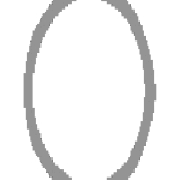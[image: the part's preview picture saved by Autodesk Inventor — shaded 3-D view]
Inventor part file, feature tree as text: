
AUTODESK INVENTOR PART (.ipt)
format: ipt  version: 2021 (Build 250183000, 183)  size: 125,952 bytes
history: native  units: in
note: dims shown in document units (in); Inventor stores cm internally (conversion verified against a paired STEP export)
features: other x4, plane x3, sketch x3, split x2
ambient origin geometry x8: Origin, YZ Plane, XZ Plane, XY Plane, X Axis, Y Axis, Z Axis, Center Point
bodies: Solid1 (feature_tree), Body (feature_tree)
feature tree (12):
  other  "Driven Length"
  other  "Frame Generator"
  other  "Start Plane"
  other  "End Plane"
  plane  "Work Plane5"
  split  "Split1"
  plane  "Work Plane6"
  split  "Split2"
  sketch  "Sketch"  dims[d2=5.831in d4=-0.2406in d5=5.831in d6=0.12in d7=0.0in d10=90.0deg d9=6.0716in]
  sketch  "Sketch4"  dims[d0=1.0in]
  plane  "Work Plane4"
  sketch  "Sketch5"  dims[d1=0.065in]
